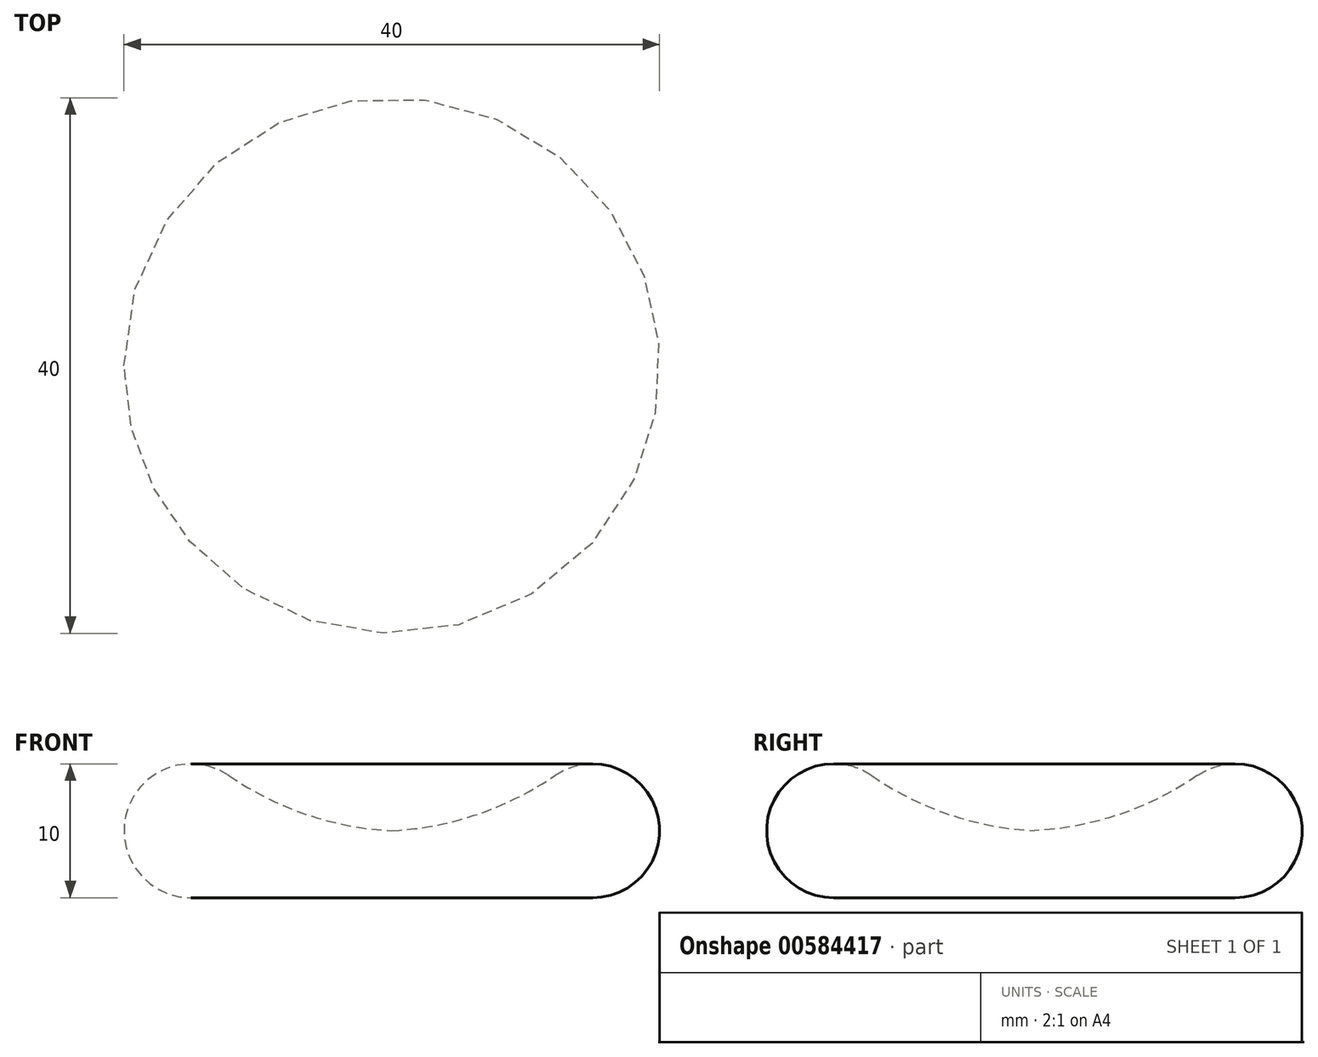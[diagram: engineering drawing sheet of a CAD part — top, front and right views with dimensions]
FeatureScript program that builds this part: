
annotation { "Feature Type Name" : "Feature", "Feature Type Description" : "" }
export const myFeature = defineFeature(function(context is Context, id is Id, definition is map)
    precondition{}
    {
        {
            var Q0;
            Q0=qCreatedBy(makeId("Front.planeOp"),FACE);
            var sketch = newSketch(context, id + "F0", { "sketchPlane" : qUnion([Q0])});
            skArc(sketch, "E0", {"start": v(-12.17, 9.12) * mm, "mid": v(-19.78, 6.48) * mm, "end": v(-15, 0) * mm});
            skArc(sketch, "E1", {"start": v(-12.17, 9.12) * mm, "mid": v(-6.37, 6.22) * mm, "end": v(0, 5) * mm});
            skLineSegment(sketch, "E2", {"start": v(-15, 0) * mm, "end": v(0, 0) * mm});
            skLineSegment(sketch, "E3", {"start": v(0, 0) * mm, "end": v(0, 5) * mm});
            skSolve(sketch);
        }
        {
            var Q0;
            Q0=makeQuery(id+"F0.imprint","IMPRINT",FACE,{"disambiguationData":[TD([[makeQuery(id+"F0.imprint","IMPRINT",EDGE,{"derivedFrom":sQuery(id+"F0.wireOp",EDGE,"E0")}),1.0]])]});
            var Q1;
            Q1=sQuery(id+"F0.wireOp",EDGE,"E3");
            revolve(context, id + "F1", {"entities" : qUnion([Q0]), "axis" : qUnion([Q1]), "revolveType" : RevolveType.FULL});
        }
    });
